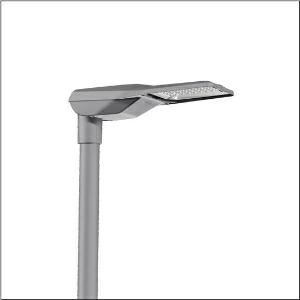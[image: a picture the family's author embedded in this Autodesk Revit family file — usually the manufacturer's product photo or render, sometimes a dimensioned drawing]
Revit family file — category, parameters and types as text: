
# Revit family: streetlight_sl_21_iq_mini___st1_5a_5xe2p41g08gb_fe87
name_source: partatom
category: Lighting Fixtures
units: mm (PartAtom-declared; Revit-internal decimal feet)

## family parameters
Cut with Voids When Loaded = No
Host = Face
Light Source = No
Part Type = Normal
Room Calculation Point = No
Round Connector Dimension = Use Diameter
Shared = No

## types (1)
- --- (1 x LED, 5810 lm, 37.1 W, 4000K)
    Apparent Load = 37 VA
    CIE Flux Codes = 22 53 95 100 100
    Color Rendering = 70
    Color Temperature = 4000K
    Default Elevation = 1800 mm
    Description = Streetlight SL 21 iQ mini, mast luminaire, primary light control with lens, of PMMA, primary optical cover: cover, of toughened safety glass, transparent, light distribution: ST1.5a, light emission: direct distribution, primary light characteristic: asymmetric, installation type: post-top, side-entry, LED, High Power LED, rated luminous flux: 5.810lm, luminous efficacy: 157lm/W, light colour: 740, colour temperature: 4000K, control: Street-Remote, Auto-Match, Temp-Guard, Lumen-Switch, Night-Set, Smart-Wire, Light-Fading, Desk-Remote (wireless, voltage-free reading and setting of iQ features in the workshop via application-optimized NFC function/RFID function), optimised constant luminous flux control (CLO 2.0), presetting dimming linear, mains connection: 220..240V, AC, 50/60Hz, start of lifetime: 37W, end of service life: 39W, reduction: 18W, luminaire housing, of diecast aluminium, powder-coated, Siteco® metallic grey (DB 702S), corrosivity category C5 mid according to DIN EN ISO 12944, please order mast flange separately, inclination adjustable: 0°, 5°, 10°, 15°, sealing non-destructively replaceable, multi-level sealing system, length: 628mm, width: 235mm, height: 110mm, mast flange for spigot size: 42mm (side-entry): 5XC10008XM4, 60/48mm (side-entry/post-top): 5XC10108XM2, 76/60mm (side-entry/post-top): 5XC10108XM1, protection rating (complete): IP66, insulation class (complete): insulation class II (safety insulation), certification: CE, ENEC, ENEC+, VDE, impact resistance: IK09, permissible operating ambient temperature for outdoor applications: -40..+50°C, standard-compliant lighting for roads and squares, packaging unit: 1 piece

Light Distribution: ST1.5a
    Height = 110 mm
    Lamp = 1 x LED
    Lamp Light Flux = 5810 lm
    Lamp Power = 37.1 W
    Lamp count = 1
    Length = 625 mm
    Luminous efficacy = 157 lm/W
    Manufacturer = Siteco
    ModVariant = No
    Model = 5XE2P41G08GB
    Number of Poles = 1
    OnlyDefault = Yes
    Power Factor = 1
    Product Name = Streetlight SL 21 iQ mini | ST1.5a
    Product group = mast luminaire | pylon top
    ProductGroupID = 6100
    Protection Class = Protection class II
    Protection Degree = IP 66
    RLX_Detail_Level = 1
    RLX_Emergency_Light_Flux = 0 lm
    RLX_Emergency_Type = 0
    RLX_Emergency_Type_DB = No
    RlxData = <blob elided: 97737 chars, md5=a1c067ef>
    Socket = socket
    Standby Power = 0 W
    System Light Flux = 5810 lm
    System Power = 37 W
    Type Comments = factory setting: luminous flux: 100 % | dim-lin: 254 | 385 mA
    Type Image = l_1003519.jpg
    URL = http://relux.com
    VarID = @adj_108973
    Voltage = 0 V
    Weight = 0.00 kg
    Width = 234 mm

## geometry (parser evidence)
native form markers: Blend x4, Sweep x8
no freeform markers — native parametric forms only
